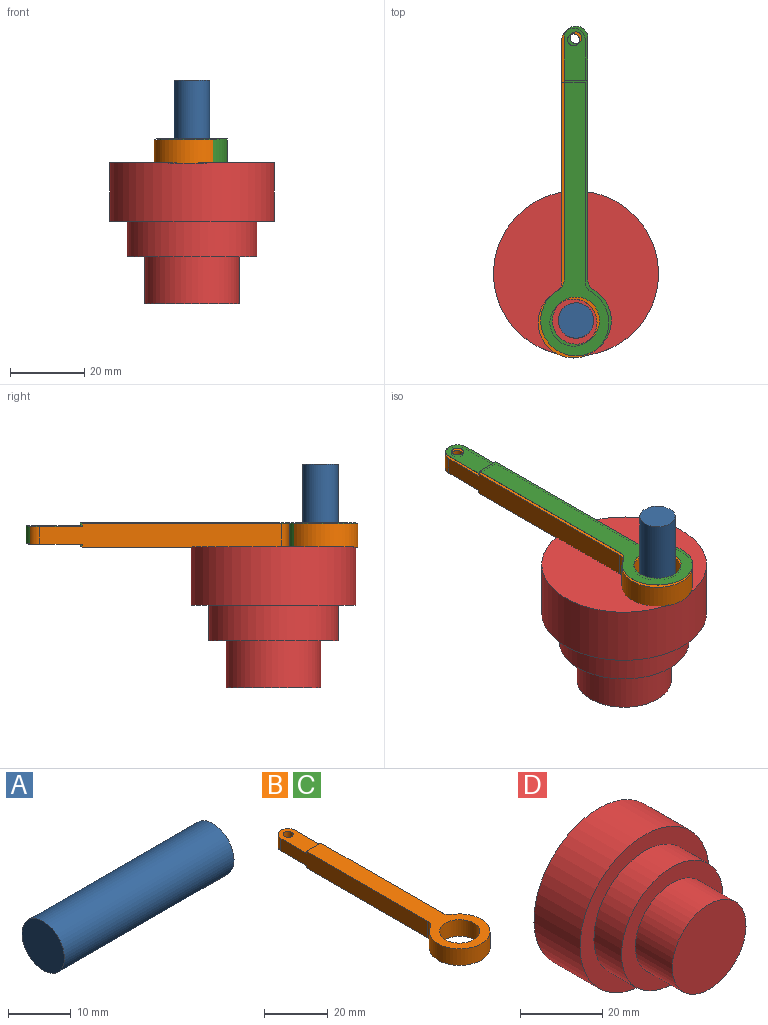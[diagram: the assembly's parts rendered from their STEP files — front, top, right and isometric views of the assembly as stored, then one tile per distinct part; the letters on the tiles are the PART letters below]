
ASSEMBLY  parts=4 mates=3
PART A: 3 faces, bbox 38.1x9.5x9.5 mm
  f0: cylinder r=4.76mm len=38.1mm, axis (-1,0,0), area 1140.1mm2, adj f1,f2
  f1: plane 9.53x9.53mm, normal (1,0,0), area 71.3mm2, adj f0
  f2: plane 9.53x9.53mm, normal (-1,0,0), area 71.3mm2, adj f0
PART B: 14 faces, bbox 19.1x88.9x6.4 mm
  f0: plane 65.2x6.35mm, normal (1,0,0), area 395.9mm2, adj f1,f3,f4,f8,f10,f11,f12,f13
  f1: cylinder r=3.17mm len=6.35mm, axis (0,0,-1), area 47.5mm2, adj f0,f5,f10,f12
  f2: cylinder r=1.59mm len=4.77mm, axis (0,0,-1), area 47.5mm2, adj f10,f12
  f3: plane 74.3x19.05mm, normal (0,0,-1), area 511.6mm2, adj f0,f5,f6,f7,f8,f9,f13
  f4: plane 74.3x19.05mm, normal (0,0,1), area 511.6mm2, adj f0,f5,f6,f7,f8,f9,f11
  f5: plane 65.2x6.35mm, normal (-1,0,0), area 395.9mm2, adj f1,f3,f4,f6,f10,f11,f12,f13
  f6: cylinder r=3.17mm len=6.35mm, axis (0,0,-1), area 21.1mm2, adj f3,f4,f5,f7
  f7: cylinder r=9.53mm len=19.05mm, axis (0,0,-1), area 316.7mm2, adj f3,f4,f6,f8
  f8: cylinder r=3.17mm len=6.35mm, axis (0,0,-1), area 21.1mm2, adj f0,f3,f4,f7
  f9: cylinder r=6.35mm len=12.7mm, axis (0,0,-1), area 253.4mm2, adj f3,f4
  f10: plane 14.61x6.35mm, normal (0,0,1), area 80.5mm2, adj f0,f1,f2,f5,f11
  f11: plane 6.35x0.79mm, normal (0,1,0), area 5mm2, adj f0,f4,f5,f10
  f12: plane 14.61x6.35mm, normal (0,0,-1), area 80.5mm2, adj f0,f1,f2,f5,f13
  f13: plane 6.35x0.79mm, normal (0,1,0), area 5mm2, adj f0,f3,f5,f12
PART C: same geometry as B
PART D: 9 faces, bbox 44.5x38.1x44.5 mm
  f0: plane 44.45x44.45mm, normal (0,1,0), area 1480.5mm2, adj f1,f8
  f1: cylinder r=22.23mm len=44.45mm, axis (0,1,0), area 2216.8mm2, adj f0,f2
  f2: plane 44.45x44.45mm, normal (0,-1,0), area 593.8mm2, adj f1,f3
  f3: cylinder r=17.46mm len=34.93mm, axis (0,1,0), area 1045.1mm2, adj f2,f4
  f4: plane 34.93x34.93mm, normal (0,-1,0), area 451.3mm2, adj f3,f5
  f5: cylinder r=12.7mm len=25.4mm, axis (0,1,0), area 1013.4mm2, adj f4,f6
  f6: plane 25.4x25.4mm, normal (0,-1,0), area 506.7mm2, adj f5
  f7: cone r=0mm half-angle=59deg, axis (0,1,0), area 83.1mm2, adj f8
  f8: cylinder r=4.76mm len=12.7mm, axis (0,1,0), area 380mm2, adj f0,f7
PLACE A rot(axis=(0,1,0),90deg) t=(0,0,19.05)mm
PLACE B t=(-0.67,-0.55,-0.17)mm
PLACE C at identity
PLACE D rot(axis=(1,0,0),90deg) t=(0,12.7,-3.18)mm
MATE cylindrical A.f0 <-> D.f7  axis (0,0,1) through (0,0,-19.05)mm
MATE planar D.f1 <-> C.f9  axis (0,0,1) through (0,12.7,-3.18)mm
MATE revolute A.f0 <-> C.f9  axis (0,0,1) through (0,0,0)mm
